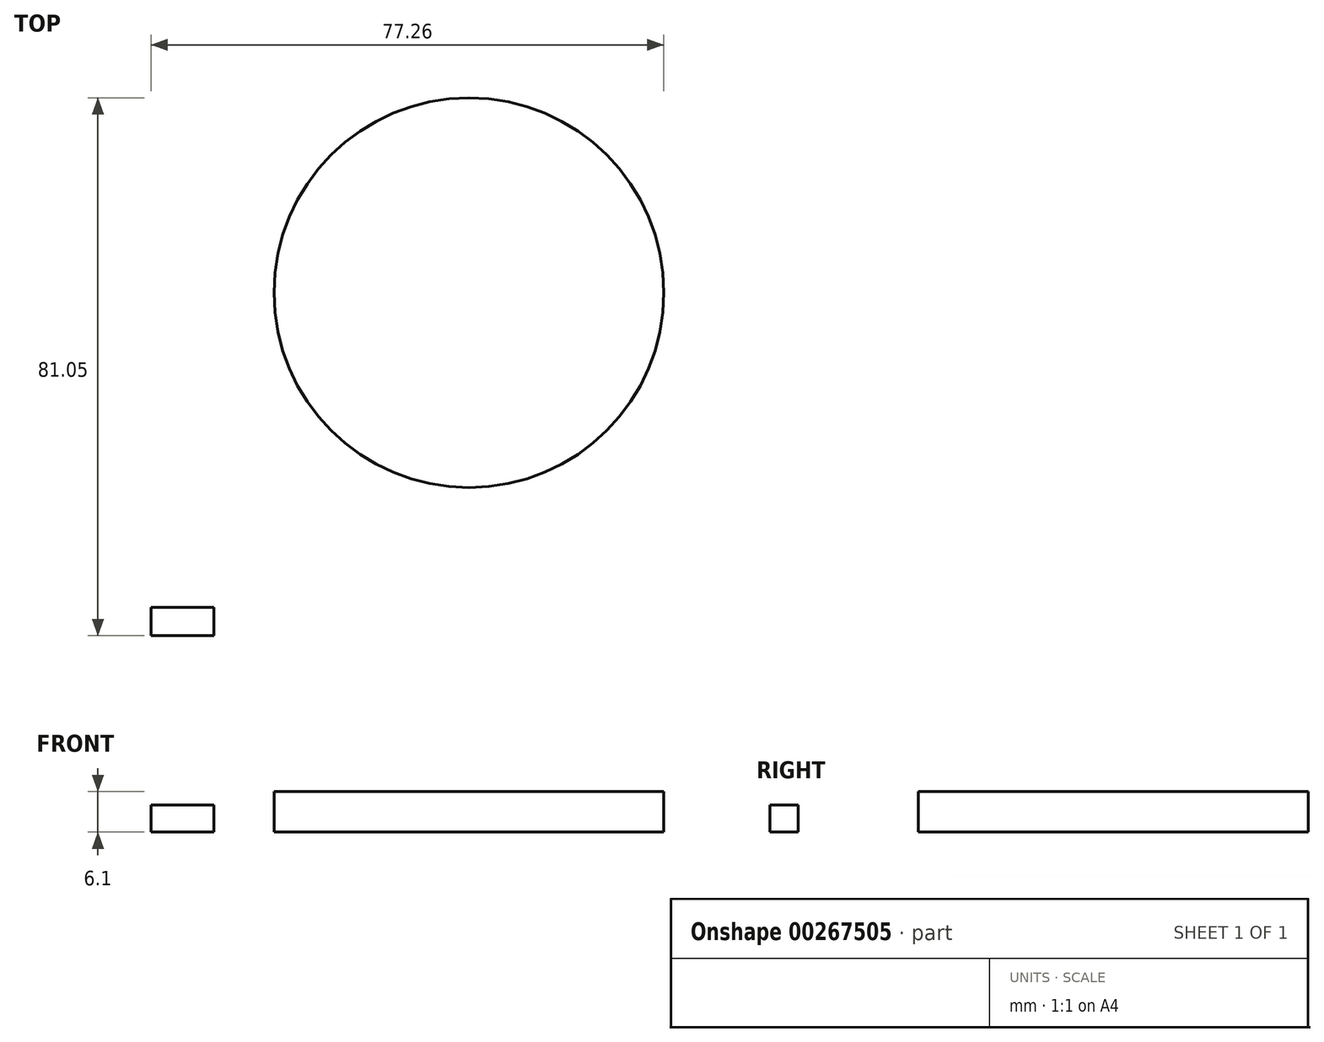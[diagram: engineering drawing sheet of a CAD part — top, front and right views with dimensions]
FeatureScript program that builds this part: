
annotation { "Feature Type Name" : "Feature", "Feature Type Description" : "" }
export const myFeature = defineFeature(function(context is Context, id is Id, definition is map)
    precondition{}
    {
        {
            var Q0;
            Q0=qCreatedBy(makeId("Top.planeOp"),FACE);
            var sketch = newSketch(context, id + "F0", { "sketchPlane" : qUnion([Q0])});
            skCircle(sketch, "E0", {"center": v(0, 0) * mm, "radius": 29.36 * mm});
            skSolve(sketch);
        }
        {
            var Q0;
            Q0 = qSketchRegion(id + "F0", true);
            extrude(context, id + "F1", {"entities" : qUnion([Q0]), "depth" : 6.1 * mm});
        }
        {
            var Q0;
            Q0=qCreatedBy(makeId("Top.planeOp"),FACE);
            var sketch = newSketch(context, id + "F2", { "sketchPlane" : qUnion([Q0])});
            skLineSegment(sketch, "E1.bottom", {"start": v(-47.9, -47.44) * mm, "end": v(-38.43, -47.44) * mm});
            skLineSegment(sketch, "E1.top", {"start": v(-47.9, -51.7) * mm, "end": v(-38.43, -51.7) * mm});
            skLineSegment(sketch, "E1.left", {"start": v(-47.9, -47.44) * mm, "end": v(-47.9, -51.7) * mm});
            skLineSegment(sketch, "E1.right", {"start": v(-38.43, -47.44) * mm, "end": v(-38.43, -51.7) * mm});
            skPoint(sketch, "E1.middle", {"position": v(-43.16, -49.57) * mm});
            skSolve(sketch);
        }
        {
            var Q0;
            Q0 = qSketchRegion(id + "F2", true);
            extrude(context, id + "F3", {"entities" : qUnion([Q0]), "depth" : 4.06 * mm});
        }
    });
